# Revit family: REVIT-MXG-2017
name_source: partatom
category: Mechanical Equipment
revit_build: Autodesk Revit 2017 (Build: 20190507_1515(x64)
units: mm (PartAtom-declared; Revit-internal decimal feet)

## family parameters
Always vertical = Yes
Cut with Voids When Loaded = No
Part Type = Normal
Room Calculation Point = No
Round Connector Dimension = Use Radius
Shared = No
Work Plane-Based = No

## types (10) — shared parameters
250 GT Visibility = No
3500 4000 GT Visibility = No
500 3000 GT Visibility = Yes
A = 8 3/8"
Air Inlet Depth = 3 1/8"
Air Inlet Diameter = 6"
Air Inlet Extension = 18 15/16"
Air Inlet Radius = 3"
Air Inlet Width = 6 3/8"
Air Inlet X = 14 7/8"
Air Inlet Y = 5 1/4"
Air Inlet Y Offset = 2 1/16"
Air Inlet Z Offset = 2 1/16"
Assembly Code = D3040400
B = 3 15/16"
Blower Motor Phase = 1
Blower Motor Voltage = 120 V
Burner Depth = 15 1/2"
Burner Height = 13 3/4"
Burner Width = 14 11/16"
Current = 2 A
Description = Maxim Series Gas Water Heater
Disclaimer = This rendering is for building modeling purposes only. Submittal/catalog is still the contract document. PVI reserves the right to change design and specification without notice.
Drain NPT = 1"
Drain Radius = 1/2"
Energy Radius = 4"
Frequency = 60 Hz
Height to Cold Inlet = 33"
Height to Drain = 25 1/2"
Height to Energy = 7"
Height to Hot Outlet = 70"
Height to Relief = 70 5/8"
Manufacturer = PVI Industries, LLC
Phase = 1
RandD Angle = 45.00°
Relief Valve NPT = 3/4"
Relief Valve Radius = 3/8"
URL = www.pvi.com
Unit Height = 79"
Voltage = 120 V

## per-type parameters (varying)
- 54 L 250A-MXL: 500-3000 GIY=3 5/8"; Apparent Load=1200 VA; Blower Motor Current=8 A; Blower Motor HP=0.3333; Cold Water Extension=23 1/2"; Cold Water NPT=2"; Cold Water Radius=1"; Control Panel Extension=29 1/2"; Drain Extension=26 3/8"; Energy Extension=25"; Flue Diameter=8"; Flue Radius=4"; Front Skid Extension=67 1/2"; GT Conn Z=47 5/8"; GT Z=27"; Gas Conn X=36 7/8"; Gas Conn Y=13 5/8"; Gas Inlet NPT=1"; Gas Inlet Radius=1/2"; Gas Inlet X=16 7/8"; Gas Inlet Y=3 5/8"; Gas Inlet Z=22 5/8"; Hot Water Extension=23 1/2"; Hot Water NPT=2"; Hot Water Radius=1"; Input=540000 Btu/h; Rear Skid Extension=22 1/2"; Recovery Rate 40F to 140F=530 gph; Relief Extension=23 1/2"; Skid Center Dist=12 1/4"; Skid Length=45"; Skid Spacing=24 1/2"; Unit Radius=22 1/2"; Weight=1440
- 65 L 250A-MXL: 500-3000 GIY=4 1/2"; Apparent Load=1200 VA; Blower Motor Current=8 A; Blower Motor HP=0.3333; Cold Water Extension=23 1/2"; Cold Water NPT=2"; Cold Water Radius=1"; Control Panel Extension=29 1/2"; Drain Extension=26 3/8"; Energy Extension=25"; Flue Diameter=10"; Flue Radius=5"; Front Skid Extension=67 1/2"; GT Conn Z=52 11/16"; GT Z=27"; Gas Conn X=40 1/2"; Gas Conn Y=14 1/2"; Gas Inlet NPT=1 1/4"; Gas Inlet Radius=5/8"; Gas Inlet X=20 1/2"; Gas Inlet Y=4 1/2"; Gas Inlet Z=27 11/16"; Hot Water Extension=23 1/2"; Hot Water NPT=2"; Hot Water Radius=1"; Input=650000 Btu/h; Rear Skid Extension=22 1/2"; Recovery Rate 40F to 140F=640 gph; Relief Extension=23 1/2"; Skid Center Dist=12 1/4"; Skid Length=45"; Skid Spacing=24 1/2"; Unit Radius=22 1/2"; Weight=1487
- 54 L 125A-MXG: 500-3000 GIY=3 5/8"; Apparent Load=1200 VA; Blower Motor Current=8 A; Blower Motor HP=0.3333; Cold Water Extension=18 1/8"; Cold Water NPT=2"; Cold Water Radius=1"; Control Panel Extension=24 1/8"; Drain Extension=21"; Energy Extension=19 5/8"; Flue Diameter=8"; Flue Radius=4"; Front Skid Extension=51 5/8"; GT Conn Z=42 1/4"; GT Z=21 5/8"; Gas Conn X=36 7/8"; Gas Conn Y=13 5/8"; Gas Inlet NPT=1"; Gas Inlet Radius=1/2"; Gas Inlet X=16 7/8"; Gas Inlet Y=3 5/8"; Gas Inlet Z=22 5/8"; Hot Water Extension=18 1/8"; Hot Water NPT=2"; Hot Water Radius=1"; Input=540000 Btu/h; Rear Skid Extension=17 1/8"; Recovery Rate 40F to 140F=540 gph; Relief Extension=18 1/8"; Skid Center Dist=11 1/4"; Skid Length=34 1/2"; Skid Spacing=22 1/2"; Unit Radius=17 1/8"; Weight=1110
- 72 L 125A-MXG: 500-3000 GIY=4 1/2"; Apparent Load=1200 VA; Blower Motor Current=8 A; Blower Motor HP=0.3333; Cold Water Extension=18 1/8"; Cold Water NPT=2"; Cold Water Radius=1"; Control Panel Extension=24 1/8"; Drain Extension=21"; Energy Extension=19 5/8"; Flue Diameter=10"; Flue Radius=5"; Front Skid Extension=51 5/8"; GT Conn Z=47 5/16"; GT Z=21 5/8"; Gas Conn X=40 1/2"; Gas Conn Y=14 1/2"; Gas Inlet NPT=1 1/4"; Gas Inlet Radius=5/8"; Gas Inlet X=20 1/2"; Gas Inlet Y=4 1/2"; Gas Inlet Z=27 11/16"; Hot Water Extension=18 1/8"; Hot Water NPT=2"; Hot Water Radius=1"; Input=720000 Btu/h; Rear Skid Extension=17 1/8"; Recovery Rate 40F to 140F=720 gph; Relief Extension=18 1/8"; Skid Center Dist=11 1/4"; Skid Length=34 1/2"; Skid Spacing=22 1/2"; Unit Radius=17 1/8"; Weight=1190
- 80 L 125A-MXG: 500-3000 GIY=4 1/2"; Apparent Load=1200 VA; Blower Motor Current=8 A; Blower Motor HP=0.3333; Cold Water Extension=18 1/8"; Cold Water NPT=2"; Cold Water Radius=1"; Control Panel Extension=24 1/8"; Drain Extension=21"; Energy Extension=19 5/8"; Flue Diameter=10"; Flue Radius=5"; Front Skid Extension=51 5/8"; GT Conn Z=47 5/16"; GT Z=21 5/8"; Gas Conn X=40 1/2"; Gas Conn Y=14 1/2"; Gas Inlet NPT=1 1/4"; Gas Inlet Radius=5/8"; Gas Inlet X=20 1/2"; Gas Inlet Y=4 1/2"; Gas Inlet Z=27 11/16"; Hot Water Extension=18 1/8"; Hot Water NPT=2"; Hot Water Radius=1"; Input=800000 Btu/h; Rear Skid Extension=17 1/8"; Recovery Rate 40F to 140F=800 gph; Relief Extension=18 1/8"; Skid Center Dist=11 1/4"; Skid Length=34 1/2"; Skid Spacing=22 1/2"; Unit Radius=17 1/8"; Weight=1210
- 54 L 250A-MXG: 500-3000 GIY=3 5/8"; Apparent Load=1200 VA; Blower Motor Current=8 A; Blower Motor HP=0.3333; Cold Water Extension=23 1/2"; Cold Water NPT=2"; Cold Water Radius=1"; Control Panel Extension=29 1/2"; Drain Extension=26 3/8"; Energy Extension=25"; Flue Diameter=8"; Flue Radius=4"; Front Skid Extension=67 1/2"; GT Conn Z=47 5/8"; GT Z=27"; Gas Conn X=36 7/8"; Gas Conn Y=13 5/8"; Gas Inlet NPT=1"; Gas Inlet Radius=1/2"; Gas Inlet X=16 7/8"; Gas Inlet Y=3 5/8"; Gas Inlet Z=22 5/8"; Hot Water Extension=23 1/2"; Hot Water NPT=2"; Hot Water Radius=1"; Input=540000 Btu/h; Rear Skid Extension=22 1/2"; Recovery Rate 40F to 140F=540 gph; Relief Extension=23 1/2"; Skid Center Dist=12 1/4"; Skid Length=45"; Skid Spacing=24 1/2"; Unit Radius=22 1/2"; Weight=1440
- 72 L 250A-MXG: 500-3000 GIY=4 1/2"; Apparent Load=1200 VA; Blower Motor Current=8 A; Blower Motor HP=0.3333; Cold Water Extension=23 1/2"; Cold Water NPT=2"; Cold Water Radius=1"; Control Panel Extension=29 1/2"; Drain Extension=26 3/8"; Energy Extension=25"; Flue Diameter=10"; Flue Radius=5"; Front Skid Extension=67 1/2"; GT Conn Z=52 11/16"; GT Z=27"; Gas Conn X=40 1/2"; Gas Conn Y=14 1/2"; Gas Inlet NPT=1 1/4"; Gas Inlet Radius=5/8"; Gas Inlet X=20 1/2"; Gas Inlet Y=4 1/2"; Gas Inlet Z=27 11/16"; Hot Water Extension=23 1/2"; Hot Water NPT=2"; Hot Water Radius=1"; Input=720000 Btu/h; Rear Skid Extension=22 1/2"; Recovery Rate 40F to 140F=720 gph; Relief Extension=23 1/2"; Skid Center Dist=12 1/4"; Skid Length=45"; Skid Spacing=24 1/2"; Unit Radius=22 1/2"; Weight=1535
- 80 L 250A-MXG: 500-3000 GIY=4 1/2"; Apparent Load=1200 VA; Blower Motor Current=8 A; Blower Motor HP=0.3333; Cold Water Extension=23 1/2"; Cold Water NPT=2"; Cold Water Radius=1"; Control Panel Extension=29 1/2"; Drain Extension=26 3/8"; Energy Extension=25"; Flue Diameter=10"; Flue Radius=5"; Front Skid Extension=67 1/2"; GT Conn Z=52 11/16"; GT Z=27"; Gas Conn X=40 1/2"; Gas Conn Y=14 1/2"; Gas Inlet NPT=1 1/4"; Gas Inlet Radius=5/8"; Gas Inlet X=20 1/2"; Gas Inlet Y=4 1/2"; Gas Inlet Z=27 11/16"; Hot Water Extension=23 1/2"; Hot Water NPT=2"; Hot Water Radius=1"; Input=800000 Btu/h; Rear Skid Extension=22 1/2"; Recovery Rate 40F to 140F=800 gph; Relief Extension=23 1/2"; Skid Center Dist=12 1/4"; Skid Length=45"; Skid Spacing=24 1/2"; Unit Radius=22 1/2"; Weight=1610
- 100 L 250A-MXG: 500-3000 GIY=5 1/2"; Apparent Load=1440 VA; Blower Motor Current=10 A; Blower Motor HP=0.5; Cold Water Extension=23 1/2"; Cold Water NPT=3"; Cold Water Radius=1 1/2"; Control Panel Extension=29 1/2"; Drain Extension=26 3/8"; Energy Extension=25"; Flue Diameter=10"; Flue Radius=5"; Front Skid Extension=67 1/2"; GT Conn Z=61 7/16"; GT Z=27"; Gas Conn X=40 1/2"; Gas Conn Y=15 1/2"; Gas Inlet NPT=2"; Gas Inlet Radius=1"; Gas Inlet X=20 1/2"; Gas Inlet Y=5 1/2"; Gas Inlet Z=36 7/16"; Hot Water Extension=23 1/2"; Hot Water NPT=3"; Hot Water Radius=1 1/2"; Input=1000000 Btu/h; Rear Skid Extension=22 1/2"; Recovery Rate 40F to 140F=1000 gph; Relief Extension=23 1/2"; Skid Center Dist=12 1/4"; Skid Length=45"; Skid Spacing=24 1/2"; Unit Radius=22 1/2"; Weight=1670
- 120 L 250A-MXG: 500-3000 GIY=5 1/2"; Apparent Load=1440 VA; Blower Motor Current=10 A; Blower Motor HP=0.5; Cold Water Extension=23 1/2"; Cold Water NPT=3"; Cold Water Radius=1 1/2"; Control Panel Extension=29 1/2"; Drain Extension=26 3/8"; Energy Extension=25"; Flue Diameter=12"; Flue Radius=6"; Front Skid Extension=67 1/2"; GT Conn Z=61 7/16"; GT Z=27"; Gas Conn X=40 1/2"; Gas Conn Y=15 1/2"; Gas Inlet NPT=2"; Gas Inlet Radius=1"; Gas Inlet X=20 1/2"; Gas Inlet Y=5 1/2"; Gas Inlet Z=36 7/16"; Hot Water Extension=23 1/2"; Hot Water NPT=3"; Hot Water Radius=1 1/2"; Input=1200000 Btu/h; Rear Skid Extension=22 1/2"; Recovery Rate 40F to 140F=1200 gph; Relief Extension=23 1/2"; Skid Center Dist=12 1/4"; Skid Length=45"; Skid Spacing=24 1/2"; Unit Radius=22 1/2"; Weight=1760

note: column(s) folded — value = type name in every type: Model

## geometry (parser evidence)
native form markers: Blend x2, Sweep x3
no freeform markers — native parametric forms only
